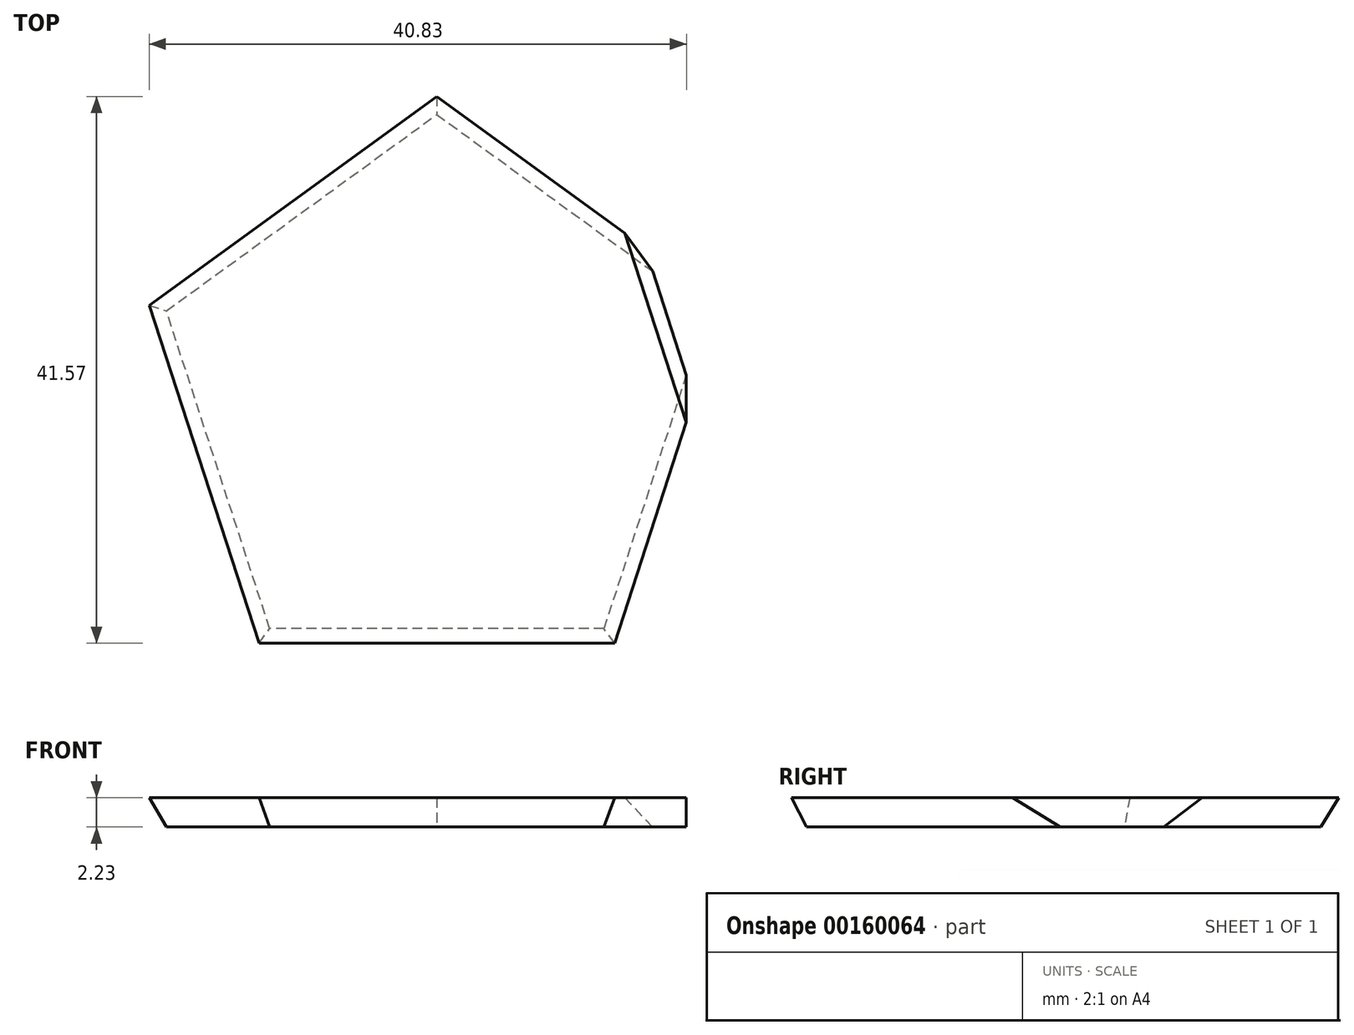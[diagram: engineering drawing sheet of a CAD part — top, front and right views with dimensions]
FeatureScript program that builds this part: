
annotation { "Feature Type Name" : "Feature", "Feature Type Description" : "" }
export const myFeature = defineFeature(function(context is Context, id is Id, definition is map)
    precondition{}
    {
        {
            var Q0;
            Q0=qCreatedBy(makeId("Top.planeOp"),FACE);
            var sketch = newSketch(context, id + "F0", { "sketchPlane" : qUnion([Q0])});
            skCircle(sketch, "E0.cCircle", {"center": v(0, 0) * mm, "radius": 17.48 * mm, "construction": true});
            skLineSegment(sketch, "E0.0", {"start": v(20.55, 6.68) * mm, "end": v(12.7, -17.48) * mm});
            skLineSegment(sketch, "E0.1", {"start": v(12.7, -17.48) * mm, "end": v(-12.7, -17.48) * mm});
            skLineSegment(sketch, "E0.2", {"start": v(-12.7, -17.48) * mm, "end": v(-20.55, 6.68) * mm});
            skLineSegment(sketch, "E0.3", {"start": v(-20.55, 6.68) * mm, "end": v(0, 21.6) * mm});
            skLineSegment(sketch, "E0.4", {"start": v(0, 21.6) * mm, "end": v(20.55, 6.68) * mm});
            skPoint(sketch, "E0.0.midPoint", {"position": v(16.62, -5.4) * mm});
            skSolve(sketch);
        }
        {
            var Q0;
            Q0 = qSketchRegion(id + "F0", true);
            extrude(context, id + "F1", {"entities" : qUnion([Q0]), "depth" : ((1 / sin(36 * degree)) * (sin(18 * degree) + 1)) * mm, "hasDraft" : true, "draftAngle" : acos(-1 / sqrt(5)) - 90 * degree});
        }
        {
            var Q0;
            Q0=makeQuery(id+"F1.opExtrude","CAP_FACE",FACE,{"disambiguationData":[OSD([sQuery(id+"F0.wireOp",EDGE,"E0.0"),sQuery(id+"F0.wireOp",EDGE,"E0.1"),sQuery(id+"F0.wireOp",EDGE,"E0.2"),sQuery(id+"F0.wireOp",EDGE,"E0.3"),sQuery(id+"F0.wireOp",EDGE,"E0.4")])],"isStart":false});
            var sketch = newSketch(context, id + "F2", { "sketchPlane" : qUnion([Q0])});
            skCircle(sketch, "E1.cCircle", {"center": v(0, 0) * mm, "radius": 17.48 * mm, "construction": true});
            skLineSegment(sketch, "E1.0", {"start": v(12.7, 17.48) * mm, "end": v(20.55, -6.68) * mm});
            skLineSegment(sketch, "E1.1", {"start": v(20.55, -6.68) * mm, "end": v(0, -21.6) * mm});
            skLineSegment(sketch, "E1.2", {"start": v(0, -21.6) * mm, "end": v(-20.55, -6.68) * mm});
            skLineSegment(sketch, "E1.3", {"start": v(-20.55, -6.68) * mm, "end": v(-12.7, 17.48) * mm});
            skLineSegment(sketch, "E1.4", {"start": v(-12.7, 17.48) * mm, "end": v(12.7, 17.48) * mm});
            skPoint(sketch, "E1.0.midPoint", {"position": v(16.62, 5.4) * mm});
            skSolve(sketch);
        }
        {
            var Q0;
            Q0=makeQuery(id+"F2.imprint","IMPRINT",FACE,{"disambiguationData":[TD([[makeQuery(id+"F2.imprint","IMPRINT",EDGE,{"derivedFrom":sQuery(id+"F2.wireOp",EDGE,"E1.0")}),1.0]])]});
            extrude(context, id + "F3", {"entities" : qUnion([Q0]), "operationType" : NewBodyOperationType.REMOVE, "oppositeDirection" : true, "depth" : ((1 / sin(36 * degree)) * (sin(18 * degree) + 1)) * mm, "hasDraft" : true, "draftAngle" : acos(-1 / sqrt(5)) - 90 * degree, "draftPullDirection" : true});
        }
    });
